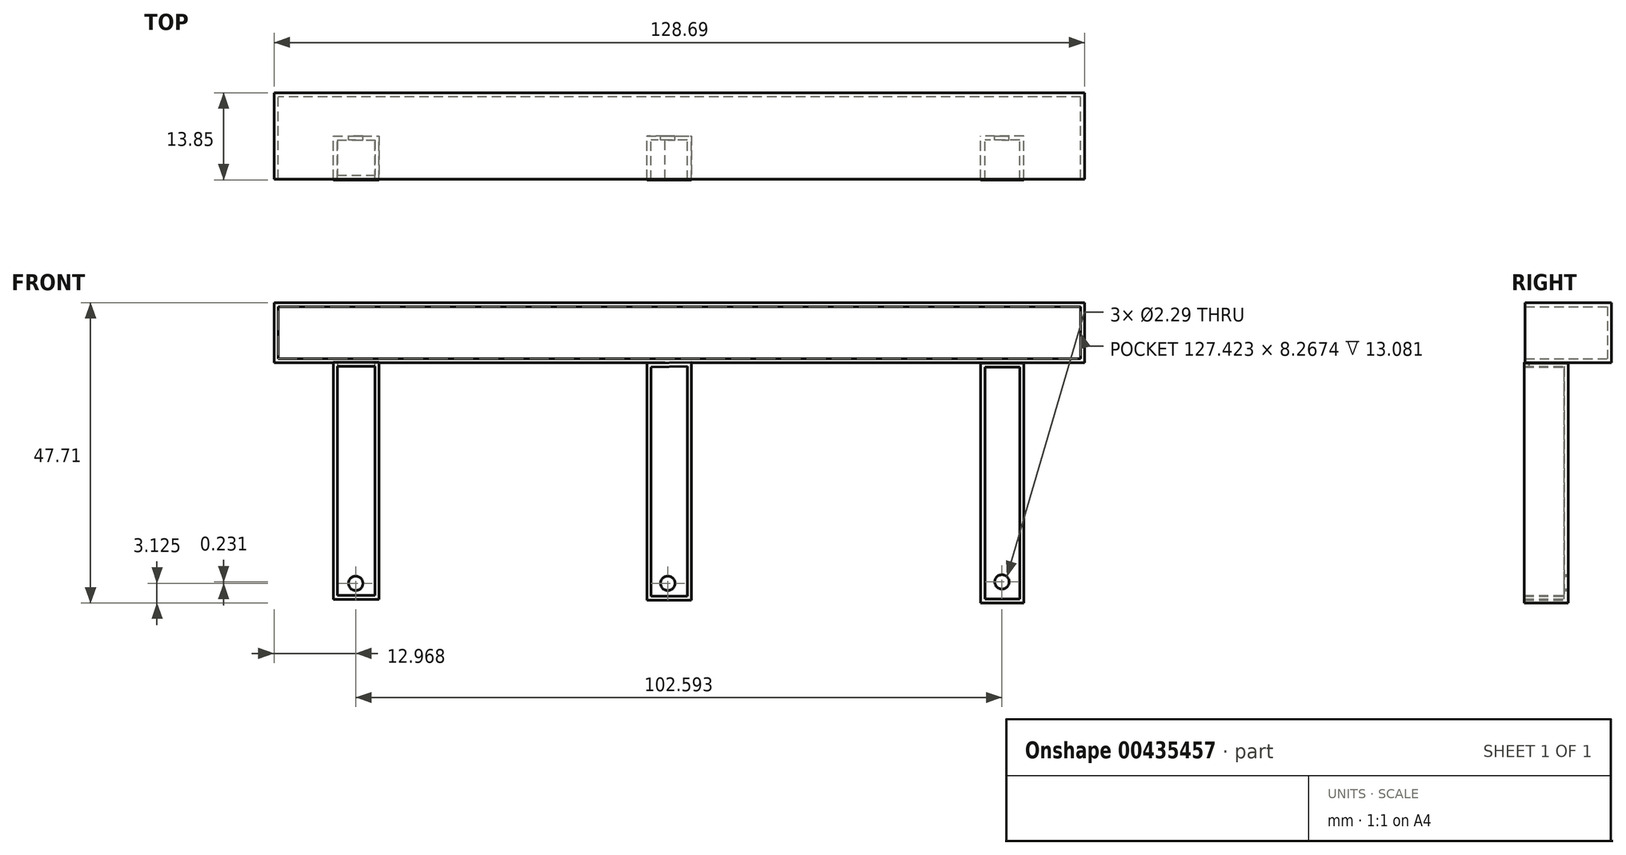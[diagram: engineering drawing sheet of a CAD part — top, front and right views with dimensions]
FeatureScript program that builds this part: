
annotation { "Feature Type Name" : "Feature", "Feature Type Description" : "" }
export const myFeature = defineFeature(function(context is Context, id is Id, definition is map)
    precondition{}
    {
        {
            var Q0;
            Q0=qCreatedBy(makeId("Front.planeOp"),FACE);
            var sketch = newSketch(context, id + "F0", { "sketchPlane" : qUnion([Q0])});
            skLineSegment(sketch, "E0", {"start": v(-62.5, 0) * mm, "end": v(-62.5, -9.54) * mm});
            skLineSegment(sketch, "E1", {"start": v(-62.5, -9.54) * mm, "end": v(66.18, -9.54) * mm});
            skLineSegment(sketch, "E2", {"start": v(66.18, -9.54) * mm, "end": v(66.18, 0) * mm});
            skLineSegment(sketch, "E3", {"start": v(66.18, 0) * mm, "end": v(0, 0) * mm});
            skLineSegment(sketch, "E4", {"start": v(0, 0) * mm, "end": v(-62.5, 0) * mm});
            skSolve(sketch);
        }
        {
            var Q0;
            Q0=qCreatedBy(makeId("Front.planeOp"),FACE);
            var sketch = newSketch(context, id + "F1", { "sketchPlane" : qUnion([Q0])});
            skLineSegment(sketch, "E5", {"start": v(-53.12, -9.5) * mm, "end": v(-53.12, -47.14) * mm});
            skLineSegment(sketch, "E6", {"start": v(-53.12, -47.14) * mm, "end": v(-45.86, -47.14) * mm});
            skLineSegment(sketch, "E7", {"start": v(-45.86, -47.14) * mm, "end": v(-45.86, -9.5) * mm});
            skLineSegment(sketch, "E8", {"start": v(-45.86, -9.5) * mm, "end": v(-53.12, -9.5) * mm});
            skSolve(sketch);
        }
        {
            var Q0;
            Q0=qCreatedBy(makeId("Front.planeOp"),FACE);
            var sketch = newSketch(context, id + "F2", { "sketchPlane" : qUnion([Q0])});
            skLineSegment(sketch, "E9", {"start": v(-3.33, -9.6) * mm, "end": v(-3.33, -47.27) * mm});
            skLineSegment(sketch, "E10", {"start": v(-3.33, -47.27) * mm, "end": v(3.73, -47.27) * mm});
            skLineSegment(sketch, "E11", {"start": v(3.73, -47.27) * mm, "end": v(3.73, -9.46) * mm});
            skLineSegment(sketch, "E12", {"start": v(3.73, -9.46) * mm, "end": v(-3.33, -9.6) * mm});
            skSolve(sketch);
        }
        {
            var Q0;
            Q0=qCreatedBy(makeId("Front.planeOp"),FACE);
            var sketch = newSketch(context, id + "F3", { "sketchPlane" : qUnion([Q0])});
            skLineSegment(sketch, "E13", {"start": v(49.69, -9.6) * mm, "end": v(49.69, -47.71) * mm});
            skLineSegment(sketch, "E14", {"start": v(49.69, -47.71) * mm, "end": v(56.5, -47.71) * mm});
            skLineSegment(sketch, "E15", {"start": v(56.5, -47.71) * mm, "end": v(56.5, -9.6) * mm});
            skLineSegment(sketch, "E16", {"start": v(56.5, -9.6) * mm, "end": v(49.69, -9.6) * mm});
            skSolve(sketch);
        }
        {
            var Q0;
            Q0=makeQuery(id+"F0.imprint","IMPRINT",FACE,{"disambiguationData":[TD([[makeQuery(id+"F0.imprint","IMPRINT",EDGE,{"derivedFrom":sQuery(id+"F0.wireOp",EDGE,"E0")}),1.0]])]});
            extrude(context, id + "F4", {"entities" : qUnion([Q0]), "endBound" : BoundingType.SYMMETRIC, "depth" : 13.72 * mm});
        }
        {
            var Q0;
            Q0=makeQuery(id+"F4.opExtrude","CAP_FACE",FACE,{"disambiguationData":[OSD([sQuery(id+"F1.wireOp",EDGE,"E5"),sQuery(id+"F1.wireOp",EDGE,"E6"),sQuery(id+"F1.wireOp",EDGE,"E7"),sQuery(id+"F1.wireOp",EDGE,"E8")])],"isStart":false});
            var Q1;
            Q1=makeQuery(id+"F4.opExtrude","CAP_FACE",FACE,{"disambiguationData":[OSD([sQuery(id+"F2.wireOp",EDGE,"E9"),sQuery(id+"F2.wireOp",EDGE,"E10"),sQuery(id+"F2.wireOp",EDGE,"E11"),sQuery(id+"F2.wireOp",EDGE,"E12")])],"isStart":false});
            var Q2;
            Q2=makeQuery(id+"F4.opExtrude","CAP_FACE",FACE,{"disambiguationData":[OSD([sQuery(id+"F3.wireOp",EDGE,"E13"),sQuery(id+"F3.wireOp",EDGE,"E14"),sQuery(id+"F3.wireOp",EDGE,"E15"),sQuery(id+"F3.wireOp",EDGE,"E16")])],"isStart":false});
            var Q3;
            Q3=makeQuery(id+"F4.opExtrude","CAP_FACE",FACE,{"disambiguationData":[OSD([sQuery(id+"F0.wireOp",EDGE,"E0"),sQuery(id+"F0.wireOp",EDGE,"E1"),sQuery(id+"F0.wireOp",EDGE,"E2"),sQuery(id+"F0.wireOp",EDGE,"E3"),sQuery(id+"F0.wireOp",EDGE,"E4")])],"isStart":false});
            shell(context, id + "F5", {"entities" : qUnion([Q0, Q1, Q2, Q3]), "thickness" : 0.64 * mm});
        }
        {
            var Q0;
            Q0=makeQuery(id+"F1.imprint","IMPRINT",FACE,{"disambiguationData":[TD([[makeQuery(id+"F1.imprint","IMPRINT",EDGE,{"derivedFrom":sQuery(id+"F1.wireOp",EDGE,"E5")}),1.0]])]});
            var Q1;
            Q1=makeQuery(id+"F3.imprint","IMPRINT",FACE,{"disambiguationData":[TD([[makeQuery(id+"F3.imprint","IMPRINT",EDGE,{"derivedFrom":sQuery(id+"F3.wireOp",EDGE,"E13")}),1.0]])]});
            var Q2;
            Q2=makeQuery(id+"F2.imprint","IMPRINT",FACE,{"disambiguationData":[TD([[makeQuery(id+"F2.imprint","IMPRINT",EDGE,{"derivedFrom":sQuery(id+"F2.wireOp",EDGE,"E9")}),1.0]])]});
            extrude(context, id + "F6", {"entities" : qUnion([Q0, Q1, Q2]), "operationType" : NewBodyOperationType.ADD, "depth" : 6.98 * mm});
        }
        {
            var Q0;
            Q0=makeQuery(id+"F6.opExtrude","CAP_FACE",FACE,{"disambiguationData":[OSD([sQuery(id+"F1.wireOp",EDGE,"E5"),sQuery(id+"F1.wireOp",EDGE,"E6"),sQuery(id+"F1.wireOp",EDGE,"E7"),sQuery(id+"F1.wireOp",EDGE,"E8")])],"isStart":false});
            var Q1;
            Q1=makeQuery(id+"F6.opExtrude","CAP_FACE",FACE,{"disambiguationData":[OSD([sQuery(id+"F2.wireOp",EDGE,"E9"),sQuery(id+"F2.wireOp",EDGE,"E10"),sQuery(id+"F2.wireOp",EDGE,"E11"),sQuery(id+"F2.wireOp",EDGE,"E12")])],"isStart":false});
            var Q2;
            Q2=makeQuery(id+"F6.opExtrude","CAP_FACE",FACE,{"disambiguationData":[OSD([sQuery(id+"F3.wireOp",EDGE,"E13"),sQuery(id+"F3.wireOp",EDGE,"E14"),sQuery(id+"F3.wireOp",EDGE,"E15"),sQuery(id+"F3.wireOp",EDGE,"E16")])],"isStart":false});
            shell(context, id + "F7", {"entities" : qUnion([Q0, Q1, Q2]), "thickness" : 0.64 * mm});
        }
        {
            var Q0;
            Q0=qCreatedBy(makeId("Front.planeOp"),FACE);
            var sketch = newSketch(context, id + "F8", { "sketchPlane" : qUnion([Q0])});
            skPoint(sketch, "E17", {"position": v(53.03, -44.51) * mm});
            skPoint(sketch, "E18", {"position": v(0, -44.58) * mm});
            skPoint(sketch, "E19", {"position": v(-49.54, -44.58) * mm});
            skSolve(sketch);
        }
        {
            var Q0;
            Q0=sQuery(id+"F8.wireOp",VERTEX,"E17");
            var Q1;
            Q1=sQuery(id+"F8.wireOp",VERTEX,"E18");
            var Q2;
            Q2=sQuery(id+"F8.wireOp",VERTEX,"E19");
            var Q3;
            Q3=makeQuery(id+"F4.opExtrude","SWEPT_BODY",BODY,{"disambiguationData":[OSD([sQuery(id+"F0.wireOp",EDGE,"E0"),sQuery(id+"F0.wireOp",EDGE,"E1"),sQuery(id+"F0.wireOp",EDGE,"E2"),sQuery(id+"F0.wireOp",EDGE,"E3"),sQuery(id+"F0.wireOp",EDGE,"E4")])]});
            hole(context, id + "F9", {"style" : HoleStyle.SIMPLE, "endStyle" : HoleEndStyle.THROUGH, "oppositeDirection" : true, "holeDiameter" : 2.3 * mm, "isTappedThrough" : true, "tappedDepth" : 12.7 * mm, "tapClearance" : 3, "locations" : qUnion([Q0, Q1, Q2]), "scope" : qUnion([Q3])});
        }
        {
            var Q0;
            Q0=qCreatedBy(makeId("Front.planeOp"),FACE);
            var sketch = newSketch(context, id + "F10", { "sketchPlane" : qUnion([Q0])});
            skPoint(sketch, "E20", {"position": v(53.05, -44.35) * mm});
            skSolve(sketch);
        }
        {
            var Q0;
            Q0=sQuery(id+"F10.wireOp",VERTEX,"E20");
            var Q1;
            Q1=makeQuery(id+"F6.opExtrude","SWEPT_BODY",BODY,{"disambiguationData":[OSD([sQuery(id+"F3.wireOp",EDGE,"E13"),sQuery(id+"F3.wireOp",EDGE,"E14"),sQuery(id+"F3.wireOp",EDGE,"E15"),sQuery(id+"F3.wireOp",EDGE,"E16")])]});
            hole(context, id + "F11", {"style" : HoleStyle.SIMPLE, "endStyle" : HoleEndStyle.THROUGH, "oppositeDirection" : true, "holeDiameter" : 2.3 * mm, "isTappedThrough" : true, "tappedDepth" : 12.7 * mm, "tapClearance" : 3, "locations" : qUnion([Q0]), "scope" : qUnion([Q1])});
        }
    });
